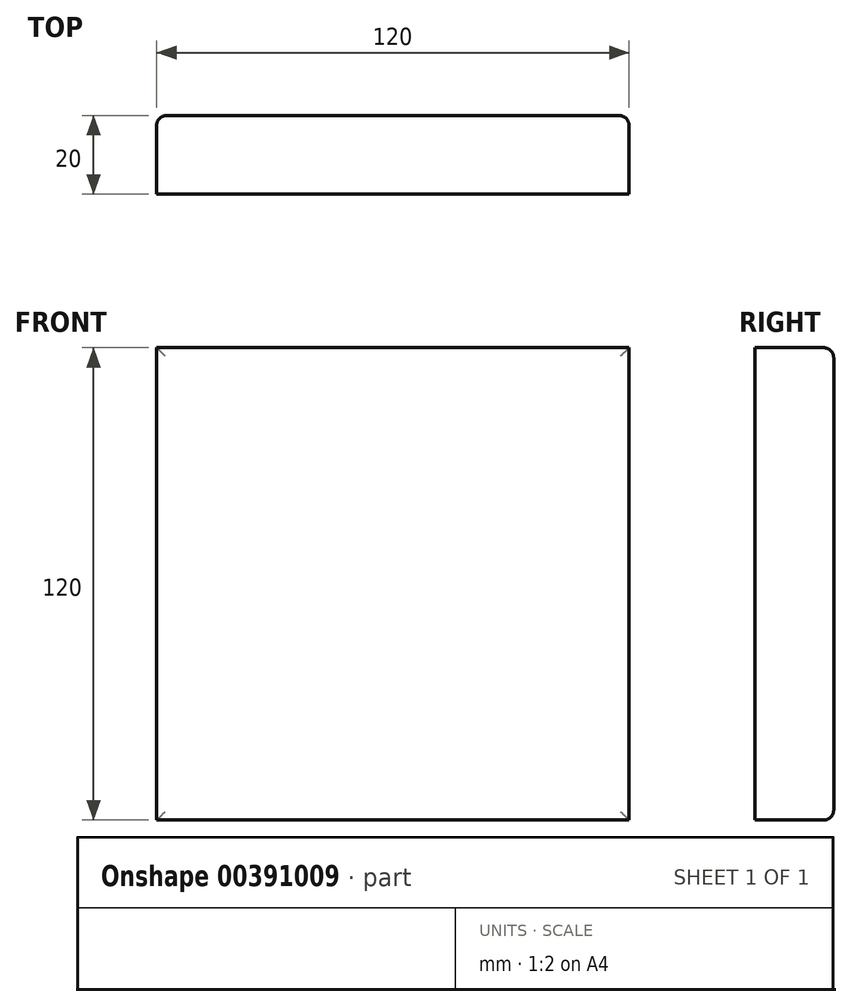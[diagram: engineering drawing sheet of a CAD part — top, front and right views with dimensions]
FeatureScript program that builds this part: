
annotation { "Feature Type Name" : "Feature", "Feature Type Description" : "" }
export const myFeature = defineFeature(function(context is Context, id is Id, definition is map)
    precondition{}
    {
        {
            var Q0;
            Q0=qCreatedBy(makeId("Front.planeOp"),FACE);
            var sketch = newSketch(context, id + "F0", { "sketchPlane" : qUnion([Q0])});
            skLineSegment(sketch, "E0.bottom", {"start": v(60, 60) * mm, "end": v(-60, 60) * mm});
            skLineSegment(sketch, "E0.top", {"start": v(60, -60) * mm, "end": v(-60, -60) * mm});
            skLineSegment(sketch, "E0.left", {"start": v(60, 60) * mm, "end": v(60, -60) * mm});
            skLineSegment(sketch, "E0.right", {"start": v(-60, 60) * mm, "end": v(-60, -60) * mm});
            skPoint(sketch, "E0.middle", {"position": v(0, 0) * mm});
            skSolve(sketch);
        }
        {
            var Q0;
            Q0=makeQuery(id+"F0.imprint","IMPRINT",FACE,{"disambiguationData":[TD([[makeQuery(id+"F0.imprint","IMPRINT",EDGE,{"derivedFrom":sQuery(id+"F0.wireOp",EDGE,"E0.bottom")}),1.0]])]});
            extrude(context, id + "F1", {"entities" : qUnion([Q0]), "depth" : 20 * mm});
        }
        {
            var Q0;
            Q0=makeQuery(id+"F1.opExtrude","CAP_EDGE",EDGE,{"disambiguationData":[OSD([sQuery(id+"F0.wireOp",EDGE,"E0.bottom")])],"isStart":true});
            var Q1;
            Q1=makeQuery(id+"F1.opExtrude","CAP_EDGE",EDGE,{"disambiguationData":[OSD([sQuery(id+"F0.wireOp",EDGE,"E0.left")])],"isStart":true});
            var Q2;
            Q2=makeQuery(id+"F1.opExtrude","CAP_EDGE",EDGE,{"disambiguationData":[OSD([sQuery(id+"F0.wireOp",EDGE,"E0.top")])],"isStart":true});
            var Q3;
            Q3=makeQuery(id+"F1.opExtrude","CAP_EDGE",EDGE,{"disambiguationData":[OSD([sQuery(id+"F0.wireOp",EDGE,"E0.right")])],"isStart":true});
            fillet(context, id + "F2", {"entities" : qUnion([Q0, Q1, Q2, Q3]), "radius" : 2.5 * mm, "tangentPropagation" : true, "allowEdgeOverflow" : false});
        }
    });
